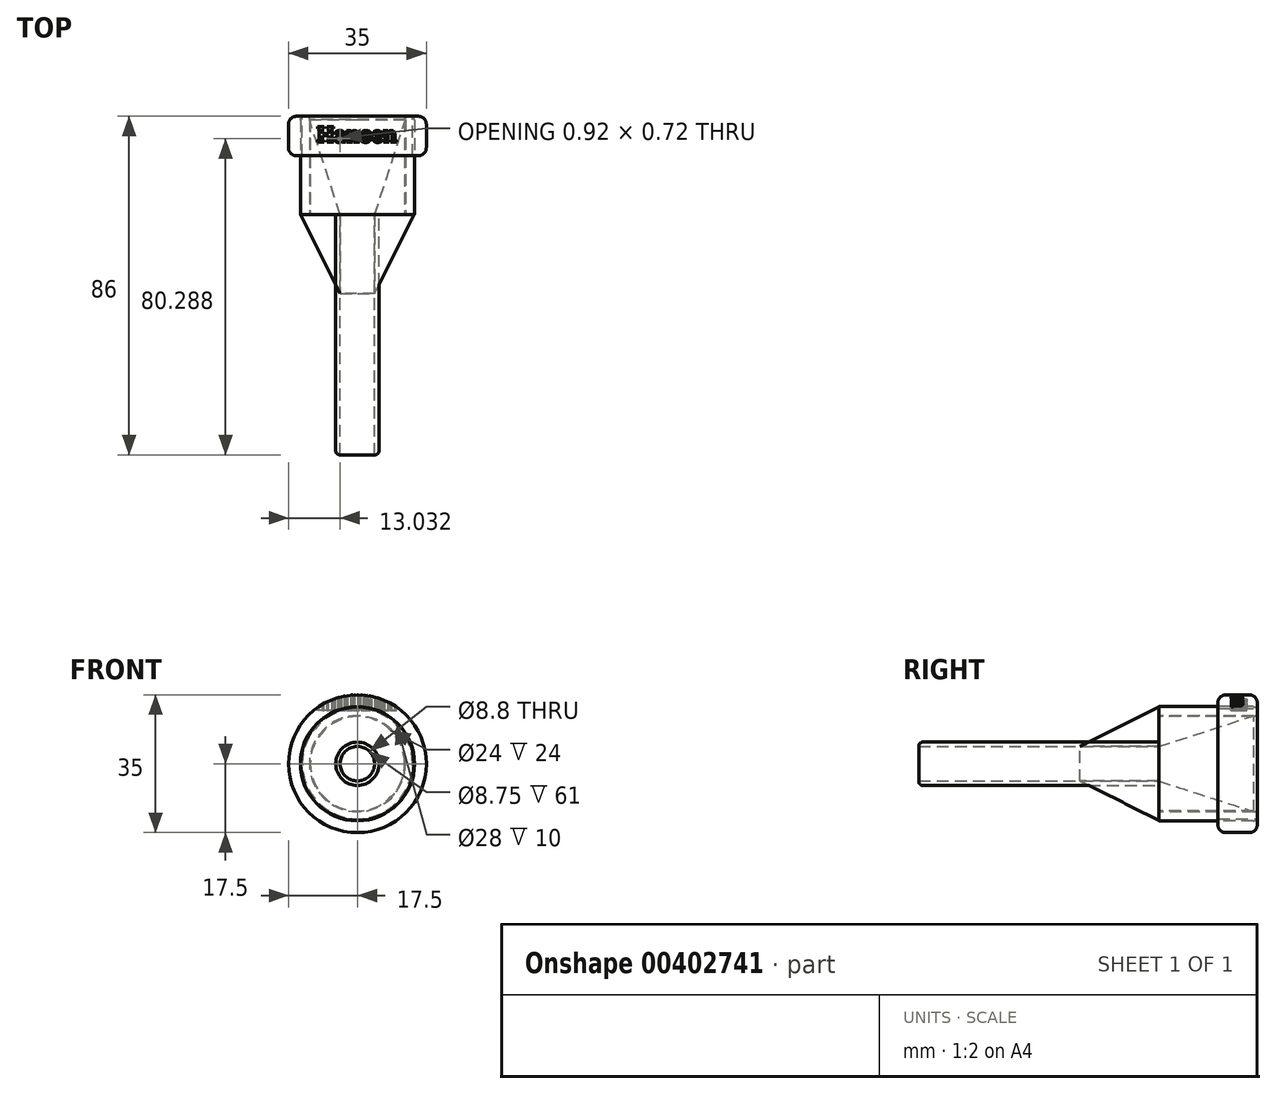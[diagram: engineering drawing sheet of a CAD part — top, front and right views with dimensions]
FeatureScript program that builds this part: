
annotation { "Feature Type Name" : "Feature", "Feature Type Description" : "" }
export const myFeature = defineFeature(function(context is Context, id is Id, definition is map)
    precondition{}
    {
        {
            var Q0;
            Q0=qCreatedBy(makeId("Front.planeOp"),FACE);
            var sketch = newSketch(context, id + "F0", { "sketchPlane" : qUnion([Q0])});
            skCircle(sketch, "E0", {"center": v(0, 0) * mm, "radius": 4.38 * mm});
            skCircle(sketch, "E1", {"center": v(0, 0) * mm, "radius": 5.5 * mm});
            skSolve(sketch);
        }
        {
            var Q0;
            Q0=makeQuery(id+"F0.imprint","IMPRINT",FACE,{"disambiguationData":[TD([[makeQuery(id+"F0.imprint","IMPRINT",EDGE,{"derivedFrom":sQuery(id+"F0.wireOp",EDGE,"E0")}),-1.0]])]});
            extrude(context, id + "F1", {"entities" : qUnion([Q0]), "depth" : 46 * mm});
        }
        {
            var Q0;
            Q0=makeQuery(id+"F1.opExtrude","CAP_FACE",FACE,{"disambiguationData":[OSD([sQuery(id+"F0.wireOp",EDGE,"E0"),sQuery(id+"F0.wireOp",EDGE,"E1")])],"isStart":true});
            var sketch = newSketch(context, id + "F2", { "sketchPlane" : qUnion([Q0])});
            skCircle(sketch, "E2", {"center": v(0, 0) * mm, "radius": 14.5 * mm});
            skCircle(sketch, "E3", {"center": v(0, 0) * mm, "radius": 12 * mm});
            skSolve(sketch);
        }
        {
            var Q0;
            Q0 = qSketchRegion(id + "F2", true);
            extrude(context, id + "F3", {"entities" : qUnion([Q0]), "depth" : 25 * mm});
        }
        {
            var Q0;
            Q0=qCreatedBy(makeId("Right.planeOp"),FACE);
            var sketch = newSketch(context, id + "F4", { "sketchPlane" : qUnion([Q0])});
            skLineSegment(sketch, "E4", {"start": v(0, 0) * mm, "end": v(0, -4.4) * mm});
            skLineSegment(sketch, "E5", {"start": v(0, -4.4) * mm, "end": v(24.17, -12.2) * mm});
            skLineSegment(sketch, "E6", {"start": v(24.17, -12.2) * mm, "end": v(0, -12.2) * mm});
            skLineSegment(sketch, "E7", {"start": v(0, -12.2) * mm, "end": v(0, -4.4) * mm});
            skLineSegment(sketch, "E8", {"start": v(0, 0) * mm, "end": v(10, 0) * mm});
            skLineSegment(sketch, "E9", {"start": v(0, -4.4) * mm, "end": v(-20, -4.4) * mm});
            skLineSegment(sketch, "E10", {"start": v(0, -4.4) * mm, "end": v(0, -14.4) * mm});
            skLineSegment(sketch, "E11", {"start": v(0, -14.4) * mm, "end": v(-20, -4.4) * mm});
            skSolve(sketch);
        }
        {
            var Q0;
            Q0=makeQuery(id+"F4.imprint","IMPRINT",FACE,{"disambiguationData":[TD([[makeQuery(id+"F4.imprint","IMPRINT",EDGE,{"derivedFrom":sQuery(id+"F4.wireOp",EDGE,"E5")}),-1.0]])]});
            var Q1;
            Q1=makeQuery(id+"F4.imprint","IMPRINT",FACE,{"disambiguationData":[TD([[makeQuery(id+"F4.imprint","IMPRINT",EDGE,{"derivedFrom":sQuery(id+"F4.wireOp",EDGE,"E7")}),1.0]])]});
            var Q2;
            {var subQ0=sQuery(id+"F4.wireOp",EDGE,"E9");Q2=makeQuery(id+"F4.imprint","IMPRINT",FACE,{"disambiguationData":[TD([[makeQuery(id+"F4.imprint","IMPRINT",EDGE,{"derivedFrom":subQ0}),1.0]])]});}
            var Q3;
            Q3=sQuery(id+"F4.wireOp",EDGE,"E8");
            revolve(context, id + "F5", {"entities" : qUnion([Q0, Q1, Q2]), "axis" : qUnion([Q3]), "revolveType" : RevolveType.FULL});
        }
        {
            var Q0;
            Q0=makeQuery(id+"F3.opExtrude","CAP_EDGE",EDGE,{"disambiguationData":[OSD([sQuery(id+"F2.wireOp",EDGE,"E2")])],"isStart":false});
            var Q1;
            Q1=makeQuery(id+"F3.opExtrude","CAP_FACE",FACE,{"disambiguationData":[OSD([sQuery(id+"F2.wireOp",EDGE,"E2"),sQuery(id+"F2.wireOp",EDGE,"E3")])],"isStart":false});
            fillet(context, id + "F6", {"entities" : qUnion([Q0, Q1]), "radius" : 1 * mm, "tangentPropagation" : true, "allowEdgeOverflow" : false});
        }
        {
            var Q0;
            Q0=makeQuery(id+"F3.opExtrude","CAP_FACE",FACE,{"disambiguationData":[OSD([sQuery(id+"F2.wireOp",EDGE,"E2"),sQuery(id+"F2.wireOp",EDGE,"E3")])],"isStart":false});
            var sketch = newSketch(context, id + "F7", { "sketchPlane" : qUnion([Q0])});
            skCircle(sketch, "E12", {"center": v(0, 0) * mm, "radius": 10.1 * mm});
            skSolve(sketch);
        }
        {
            var Q0;
            Q0=makeQuery(id+"F7.imprint","IMPRINT",FACE,{"disambiguationData":[TD([[makeQuery(id+"F7.imprint","IMPRINT",EDGE,{"derivedFrom":sQuery(id+"F7.wireOp",EDGE,"E12")}),1.0]])]});
            extrude(context, id + "F8", {"entities" : qUnion([Q0]), "operationType" : NewBodyOperationType.REMOVE, "oppositeDirection" : true, "depth" : 0.5 * mm});
        }
        {
            var Q0;
            Q0=makeQuery(id+"F3.opExtrude","CAP_FACE",FACE,{"disambiguationData":[OSD([sQuery(id+"F2.wireOp",EDGE,"E2"),sQuery(id+"F2.wireOp",EDGE,"E3")])],"isStart":false});
            var sketch = newSketch(context, id + "F9", { "sketchPlane" : qUnion([Q0])});
            skCircle(sketch, "E13", {"center": v(0, 0) * mm, "radius": 14 * mm});
            skCircle(sketch, "E14", {"center": v(0, 0) * mm, "radius": 17.5 * mm});
            skSolve(sketch);
        }
        {
            var Q0;
            Q0=makeQuery(id+"F9.imprint","IMPRINT",FACE,{"disambiguationData":[TD([[makeQuery(id+"F9.imprint","IMPRINT",EDGE,{"derivedFrom":sQuery(id+"F9.wireOp",EDGE,"E13")}),-1.0]])]});
            extrude(context, id + "F10", {"entities" : qUnion([Q0]), "oppositeDirection" : true, "depth" : 10 * mm});
        }
        {
            var Q0;
            Q0=makeQuery(id+"F10.opExtrude","CAP_EDGE",EDGE,{"disambiguationData":[OSD([sQuery(id+"F9.wireOp",EDGE,"E14")])],"isStart":true});
            var Q1;
            Q1=makeQuery(id+"F10.opExtrude","CAP_EDGE",EDGE,{"disambiguationData":[OSD([sQuery(id+"F9.wireOp",EDGE,"E14")])],"isStart":false});
            fillet(context, id + "F11", {"entities" : qUnion([Q0, Q1]), "radius" : 2 * mm, "tangentPropagation" : true, "allowEdgeOverflow" : false});
        }
        {
            var Q0;
            Q0=qCreatedBy(makeId("Top.planeOp"),FACE);
            var sketch = newSketch(context, id + "F12", { "sketchPlane" : qUnion([Q0])});
            skLineSegment(sketch, "E15.bottom", {"start": v(10, 17) * mm, "end": v(-10, 17) * mm});
            skLineSegment(sketch, "E15.top", {"start": v(10, 23) * mm, "end": v(-10, 23) * mm});
            skLineSegment(sketch, "E15.left", {"start": v(10, 17) * mm, "end": v(10, 23) * mm});
            skLineSegment(sketch, "E15.right", {"start": v(-10, 17) * mm, "end": v(-10, 23) * mm});
            skPoint(sketch, "E15.middle", {"position": v(0, 20) * mm});
            skSolve(sketch);
        }
        {
            var Q0;
            Q0=makeQuery(id+"F12.imprint","IMPRINT",FACE,{"disambiguationData":[TD([[makeQuery(id+"F12.imprint","IMPRINT",EDGE,{"derivedFrom":sQuery(id+"F12.wireOp",EDGE,"E15.bottom")}),-1.0]])]});
            cPlane(context, id + "F13", {"entities" : qUnion([Q0]), "cplaneType" : CPlaneType.OFFSET, "offset" : 16 * mm, "width" : 150 * mm, "height" : 150 * mm});
        }
        {
            var Q0;
            Q0=qCreatedBy(id+"F13.planeOp",FACE);
            var sketch = newSketch(context, id + "F14", { "sketchPlane" : qUnion([Q0])});
            skText(sketch, "E16", { "text": "Hansen", "fontName": "RobotoSlab-Bold.ttf"});
            const initialGuessF14  = {"E16": [-0.01026, 0.0184, 1, 0, 0.004]};
            skSetInitialGuess(sketch, initialGuessF14);
            skSolve(sketch);
        }
        {
            var Q0;
            Q0 = qSketchRegion(id + "F14", true);
            extrude(context, id + "F15", {"entities" : qUnion([Q0]), "operationType" : NewBodyOperationType.REMOVE, "endBound" : BoundingType.SYMMETRIC, "oppositeDirection" : true, "depth" : 5 * mm});
        }
        {
            var Q0;
            Q0=makeQuery(id+"F1.opExtrude","CAP_FACE",FACE,{"disambiguationData":[OSD([sQuery(id+"F0.wireOp",EDGE,"E0"),sQuery(id+"F0.wireOp",EDGE,"E1")])],"isStart":false});
            extrude(context, id + "F16", {"entities" : qUnion([Q0]), "operationType" : NewBodyOperationType.ADD, "depth" : 15 * mm});
        }
        {
            var Q0;
            Q0=makeQuery(id+"F16.opExtrude","CAP_EDGE",EDGE,{"disambiguationData":[OSD([sQuery(id+"F0.wireOp",EDGE,"E1")])],"isStart":false});
            fillet(context, id + "F17", {"entities" : qUnion([Q0]), "radius" : 1 * mm, "tangentPropagation" : true, "allowEdgeOverflow" : false});
        }
    });
